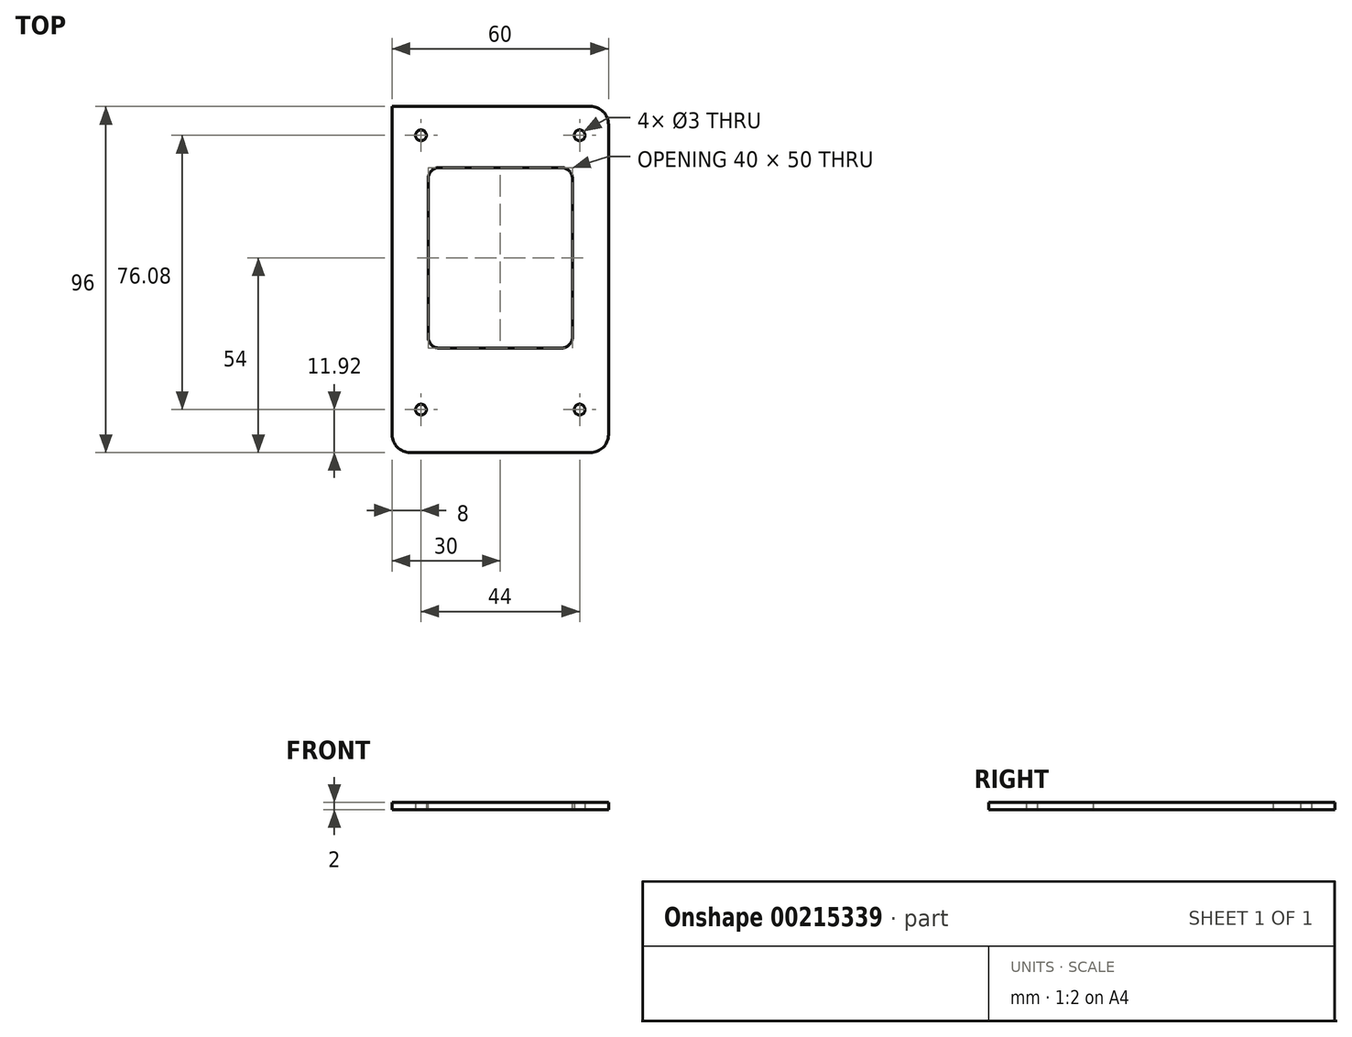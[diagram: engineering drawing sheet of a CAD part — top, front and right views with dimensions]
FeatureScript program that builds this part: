
annotation { "Feature Type Name" : "Feature", "Feature Type Description" : "" }
export const myFeature = defineFeature(function(context is Context, id is Id, definition is map)
    precondition{}
    {
        {
            var Q0;
            Q0=qCreatedBy(makeId("Top.planeOp"),FACE);
            var sketch = newSketch(context, id + "F0", { "sketchPlane" : qUnion([Q0])});
            skPoint(sketch, "E0.middle", {"position": v(0, 0) * mm});
            skCircle(sketch, "E1", {"center": v(-22, 40) * mm, "radius": 1.5 * mm});
            skCircle(sketch, "E2", {"center": v(22, 40) * mm, "radius": 1.5 * mm});
            skCircle(sketch, "E3", {"center": v(-22, -36.08) * mm, "radius": 1.5 * mm});
            skCircle(sketch, "E4", {"center": v(22, -36.08) * mm, "radius": 1.5 * mm});
            skLineSegment(sketch, "E5.bottom", {"start": v(25, -48) * mm, "end": v(-25, -48) * mm});
            skLineSegment(sketch, "E5.right", {"start": v(-30, -43) * mm, "end": v(-30, 43) * mm});
            skPoint(sketch, "E6.visualSharp", {"position": v(-30, 48) * mm});
            skPoint(sketch, "E7.visualSharp", {"position": v(30, 48) * mm});
            skLineSegment(sketch, "E8.left", {"start": v(-30, 43) * mm, "end": v(-30, 48) * mm});
            skLineSegment(sketch, "E9", {"start": v(-30, 48) * mm, "end": v(25, 48) * mm});
            skLineSegment(sketch, "E10", {"start": v(30, -43) * mm, "end": v(30, 43) * mm});
            skArc(sketch, "E11.filletArc", {"start": v(30, 43) * mm, "mid": v(28.54, 46.54) * mm, "end": v(25, 48) * mm});
            skPoint(sketch, "E12.visualSharp", {"position": v(30, -48) * mm});
            skArc(sketch, "E12.filletArc", {"start": v(25, -48) * mm, "mid": v(28.54, -46.54) * mm, "end": v(30, -43) * mm});
            skPoint(sketch, "E13.visualSharp", {"position": v(-30, -48) * mm});
            skArc(sketch, "E13.filletArc", {"start": v(-30, -43) * mm, "mid": v(-28.54, -46.54) * mm, "end": v(-25, -48) * mm});
            skSolve(sketch);
        }
        {
            var Q0;
            Q0=qSketchRegion(id+"F0",true);
            extrude(context, id + "F1", {"entities" : qUnion([Q0]), "depth" : 2 * mm});
        }
        {
            var Q0;
            Q0=makeQuery(id+"F1.opExtrude","CAP_FACE",FACE,{"disambiguationData":[OSD([sQuery(id+"F0.wireOp",EDGE,"E1"),sQuery(id+"F0.wireOp",EDGE,"E2"),sQuery(id+"F0.wireOp",EDGE,"E3"),sQuery(id+"F0.wireOp",EDGE,"E4"),sQuery(id+"F0.wireOp",EDGE,"E5.bottom"),sQuery(id+"F0.wireOp",EDGE,"E5.top"),sQuery(id+"F0.wireOp",EDGE,"E5.left"),sQuery(id+"F0.wireOp",EDGE,"E5.right")])],"isStart":false});
            var sketch = newSketch(context, id + "F2", { "sketchPlane" : qUnion([Q0])});
            skPoint(sketch, "E14.middle", {"position": v(0, 0) * mm});
            skLineSegment(sketch, "E15.bottom", {"start": v(17, 31) * mm, "end": v(-17, 31) * mm});
            skLineSegment(sketch, "E15.top", {"start": v(17, -19) * mm, "end": v(-17, -19) * mm});
            skLineSegment(sketch, "E15.left", {"start": v(20, 28) * mm, "end": v(20, -16) * mm});
            skLineSegment(sketch, "E15.right", {"start": v(-20, 28) * mm, "end": v(-20, -16) * mm});
            skPoint(sketch, "E15.middle", {"position": v(0, 6) * mm});
            skPoint(sketch, "E16.visualSharp", {"position": v(20, 31) * mm});
            skArc(sketch, "E16.filletArc", {"start": v(20, 28) * mm, "mid": v(19.12, 30.12) * mm, "end": v(17, 31) * mm});
            skPoint(sketch, "E17.visualSharp", {"position": v(-20, 31) * mm});
            skArc(sketch, "E17.filletArc", {"start": v(-17, 31) * mm, "mid": v(-19.12, 30.12) * mm, "end": v(-20, 28) * mm});
            skPoint(sketch, "E18.visualSharp", {"position": v(-20, -19) * mm});
            skArc(sketch, "E18.filletArc", {"start": v(-20, -16) * mm, "mid": v(-19.12, -18.12) * mm, "end": v(-17, -19) * mm});
            skPoint(sketch, "E19.visualSharp", {"position": v(20, -19) * mm});
            skArc(sketch, "E19.filletArc", {"start": v(17, -19) * mm, "mid": v(19.12, -18.12) * mm, "end": v(20, -16) * mm});
            skSolve(sketch);
        }
        {
            var Q0;
            Q0 = qSketchRegion(id + "F2", true);
            extrude(context, id + "F3", {"entities" : qUnion([Q0]), "operationType" : NewBodyOperationType.REMOVE, "endBound" : BoundingType.THROUGH_ALL, "oppositeDirection" : true, "depth" : 25 * mm});
        }
    });
